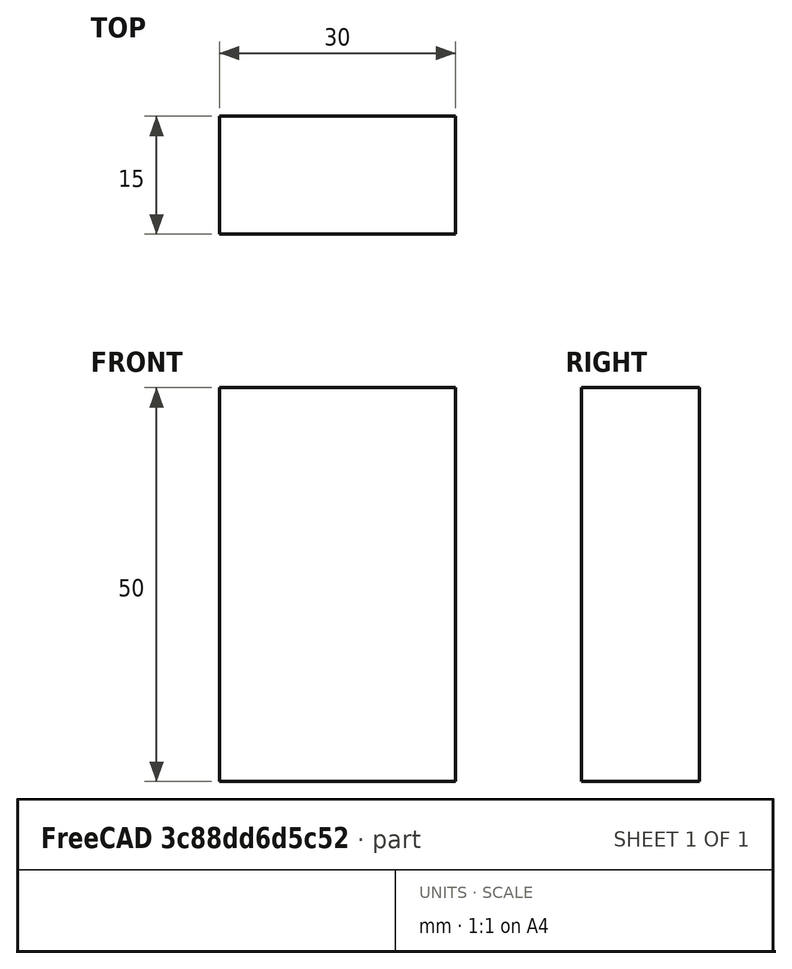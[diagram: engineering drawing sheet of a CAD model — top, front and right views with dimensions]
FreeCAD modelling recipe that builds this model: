
FCSTD DOCUMENT  (FreeCAD 0.15R4671 (Git))
Label: Flat Bar 30x15 EN10058 S235JR
License: All rights reserved
LicenseURL: http://en.wikipedia.org/wiki/All_rights_reserved
objects: Sketcher::SketchObject×1, Part::Extrusion×1
note: 2 computed .brp shape members not serialized (recipe doc carries the construction recipe); baked Part::Feature solids carry a one-line shape summary decoded from their .brp

FEATURE [Sketcher::SketchObject] Sketch
  sketch-geometry (4):
    g0: LineSegment StartX=-15 StartY=-7.5 StartZ=0 EndX=15 EndY=-7.5 EndZ=0
    g1: LineSegment StartX=15 StartY=-7.5 StartZ=0 EndX=15 EndY=7.5 EndZ=0
    g2: LineSegment StartX=15 StartY=7.5 StartZ=0 EndX=-15 EndY=7.5 EndZ=0
    g3: LineSegment StartX=-15 StartY=7.5 StartZ=0 EndX=-15 EndY=-7.5 EndZ=0
  constraints (12):
    c: Coincident(g0,g1)
    c: Coincident(g1,g2)
    c: Coincident(g2,g3)
    c: Coincident(g3,g0)
    c: Horizontal(g0)
    c: Horizontal(g2)
    c: Vertical(g1)
    c: Vertical(g3)
    c: Symmetric(g1,g2,g-2)
    c: Symmetric(g0,g1,g-1)
    c: DistanceY(g1) = 15
    c: DistanceX(g0) = 30
FEATURE [Part::Extrusion] Extrude  label="Flat Bar 30x15 EN10058 S235JR"
  Base = -> Sketch
  Dir = (0,0,50)
  Solid = true
